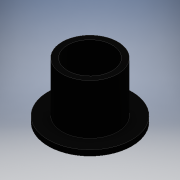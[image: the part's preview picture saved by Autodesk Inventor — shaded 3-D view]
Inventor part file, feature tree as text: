
AUTODESK INVENTOR PART (.ipt)
format: ipt  version: 2016 (Build 200138000, 138)  size: 103,424 bytes
history: native  units: mm
features: extrude x2, other x1, sketch x1
ambient origin geometry x8: Origin, YZ Plane, XZ Plane, XY Plane, X Axis, Y Axis, Z Axis, Center Point
bodies: Body1 (feature_tree)
feature tree (4):
  other  "ソリッド1"
  sketch  "スケッチ1"
  extrude  "押し出し1"  Depth=15.0mm
  extrude  "押し出し2"  Depth=10.0mm
